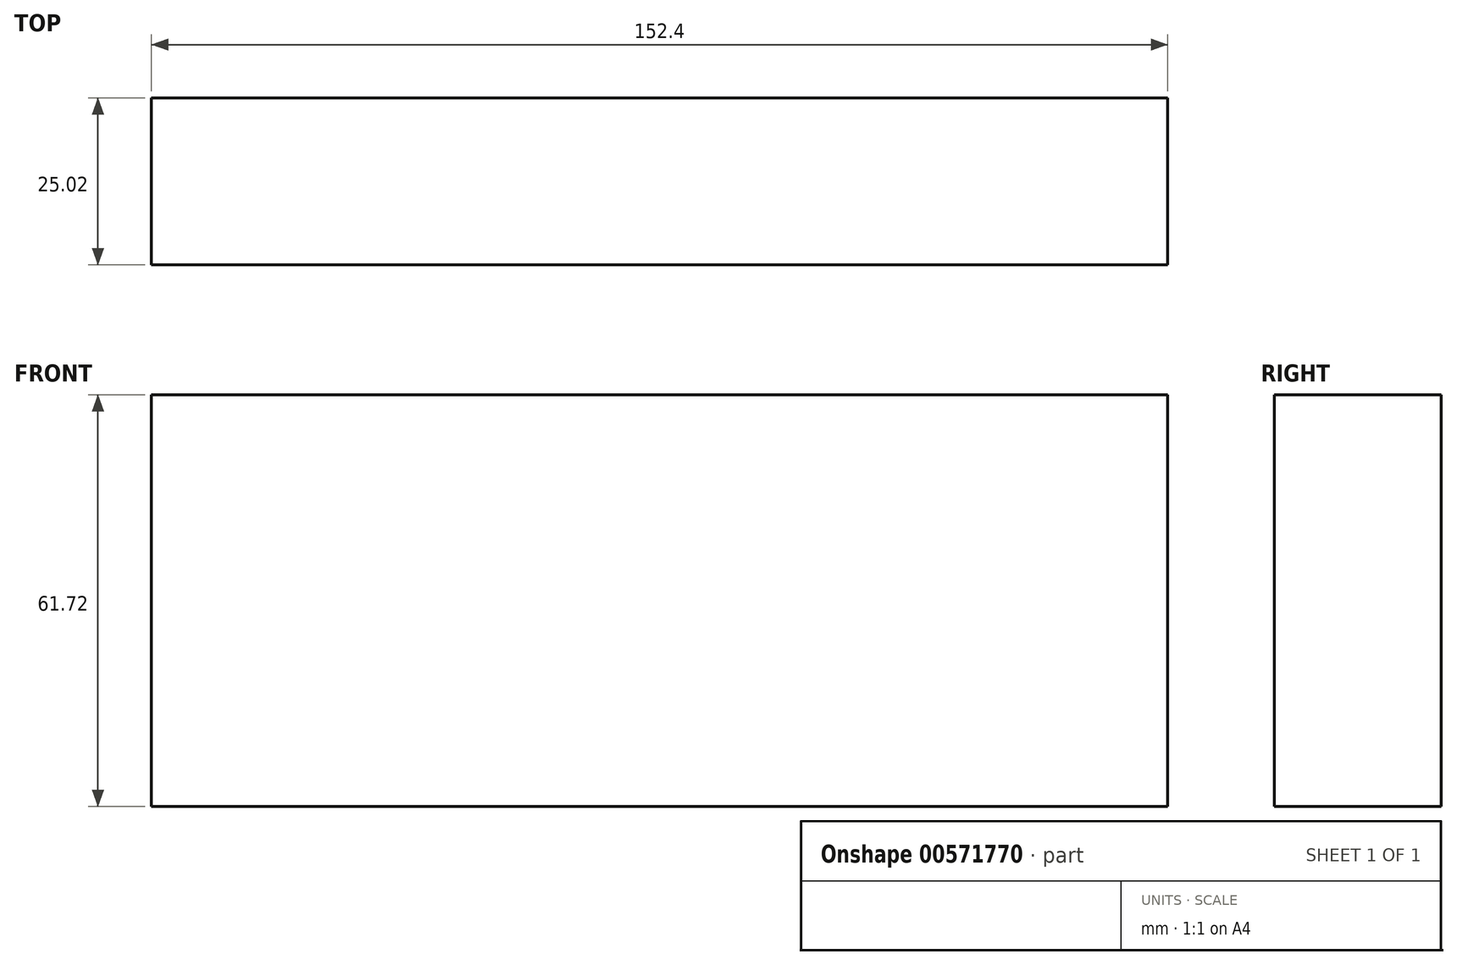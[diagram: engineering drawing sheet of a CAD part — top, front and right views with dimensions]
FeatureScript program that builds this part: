
annotation { "Feature Type Name" : "Feature", "Feature Type Description" : "" }
export const myFeature = defineFeature(function(context is Context, id is Id, definition is map)
    precondition{}
    {
        {
            var Q0;
            Q0=qCreatedBy(makeId("Front.planeOp"),FACE);
            var sketch = newSketch(context, id + "F0", { "sketchPlane" : qUnion([Q0])});
            skLineSegment(sketch, "E0.bottom", {"start": v(0, 0) * mm, "end": v(152.4, 0) * mm});
            skLineSegment(sketch, "E0.top", {"start": v(0, 61.72) * mm, "end": v(152.4, 61.72) * mm});
            skLineSegment(sketch, "E0.left", {"start": v(0, 0) * mm, "end": v(0, 61.72) * mm});
            skLineSegment(sketch, "E0.right", {"start": v(152.4, 0) * mm, "end": v(152.4, 61.72) * mm});
            skSolve(sketch);
        }
        {
            var Q0;
            Q0 = qSketchRegion(id + "F0", true);
            extrude(context, id + "F1", {"entities" : qUnion([Q0]), "depth" : 25.02 * mm, "offsetDistance" : 25.4 * mm});
        }
    });
